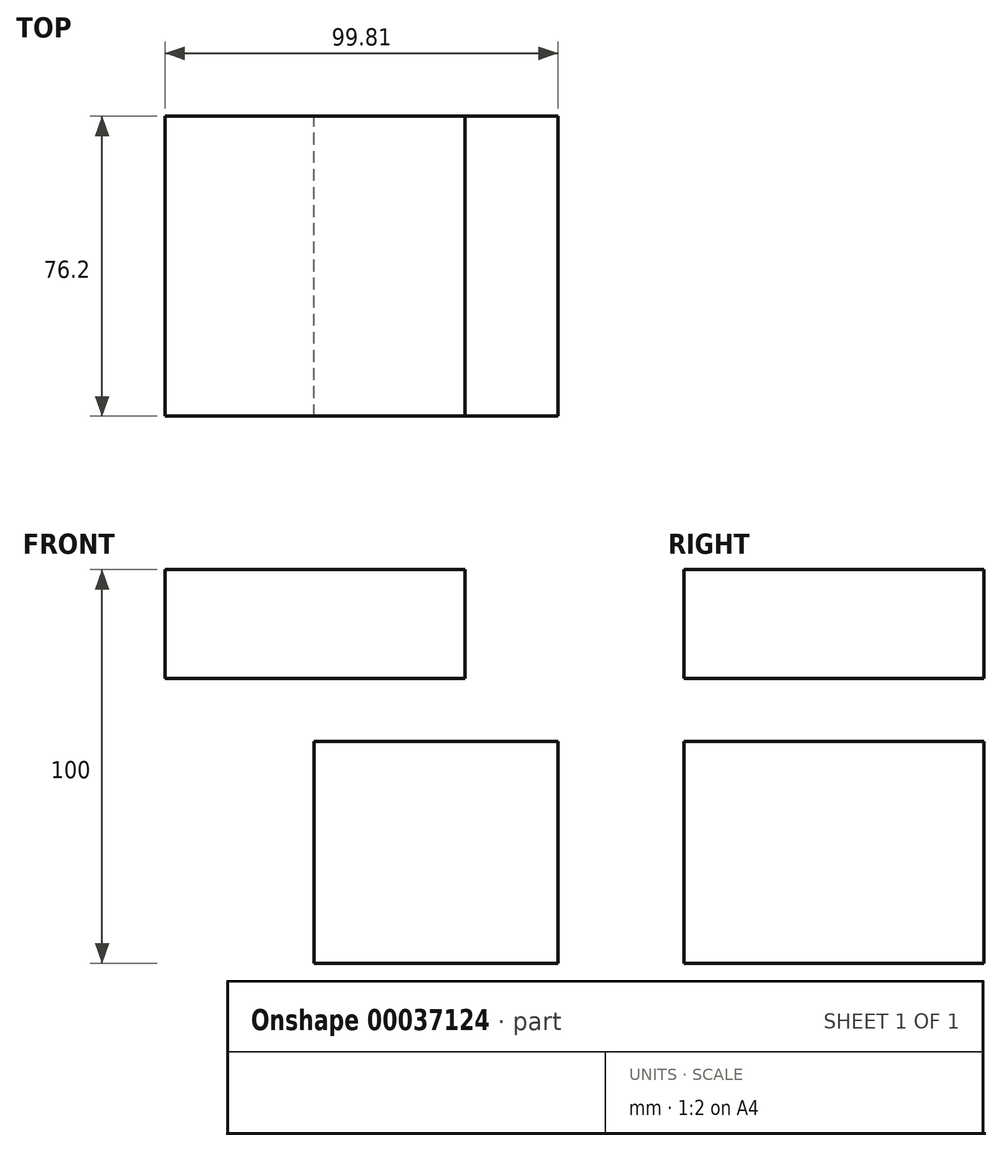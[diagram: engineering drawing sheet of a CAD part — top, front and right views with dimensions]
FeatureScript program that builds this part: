
annotation { "Feature Type Name" : "Feature", "Feature Type Description" : "" }
export const myFeature = defineFeature(function(context is Context, id is Id, definition is map)
    precondition{}
    {
        {
            var Q0;
            Q0=qCreatedBy(makeId("Front.planeOp"),FACE);
            var sketch = newSketch(context, id + "F0", { "sketchPlane" : qUnion([Q0])});
            skLineSegment(sketch, "E0.bottom", {"start": v(-29.12, -18.63) * mm, "end": v(32.88, -18.63) * mm});
            skLineSegment(sketch, "E0.top", {"start": v(-29.12, 37.73) * mm, "end": v(32.88, 37.73) * mm});
            skLineSegment(sketch, "E0.left", {"start": v(-29.12, -18.63) * mm, "end": v(-29.12, 37.73) * mm});
            skLineSegment(sketch, "E0.right", {"start": v(32.88, -18.63) * mm, "end": v(32.88, 37.73) * mm});
            skSolve(sketch);
        }
        {
            var Q0;
            Q0=makeQuery(id+"F0.imprint","IMPRINT",FACE,{"disambiguationData":[TD([[makeQuery(id+"F0.imprint","IMPRINT",EDGE,{"derivedFrom":sQuery(id+"F0.wireOp",EDGE,"E0.bottom")}),1.0]])]});
            extrude(context, id + "F1", {"entities" : qUnion([Q0]), "depth" : 76.2 * mm});
        }
        {
            var Q0;
            Q0=qCreatedBy(makeId("Front.planeOp"),FACE);
            var sketch = newSketch(context, id + "F2", { "sketchPlane" : qUnion([Q0])});
            skLineSegment(sketch, "E1.bottom", {"start": v(-66.93, 53.77) * mm, "end": v(9.24, 53.77) * mm});
            skLineSegment(sketch, "E1.top", {"start": v(-66.93, 81.37) * mm, "end": v(9.24, 81.37) * mm});
            skLineSegment(sketch, "E1.left", {"start": v(-66.93, 53.77) * mm, "end": v(-66.93, 81.37) * mm});
            skLineSegment(sketch, "E1.right", {"start": v(9.24, 53.77) * mm, "end": v(9.24, 81.37) * mm});
            skSolve(sketch);
        }
        {
            var Q0;
            Q0=makeQuery(id+"F2.imprint","IMPRINT",FACE,{"disambiguationData":[TD([[makeQuery(id+"F2.imprint","IMPRINT",EDGE,{"derivedFrom":sQuery(id+"F2.wireOp",EDGE,"E1.bottom")}),1.0]])]});
            extrude(context, id + "F3", {"entities" : qUnion([Q0]), "depth" : 76.2 * mm});
        }
    });
